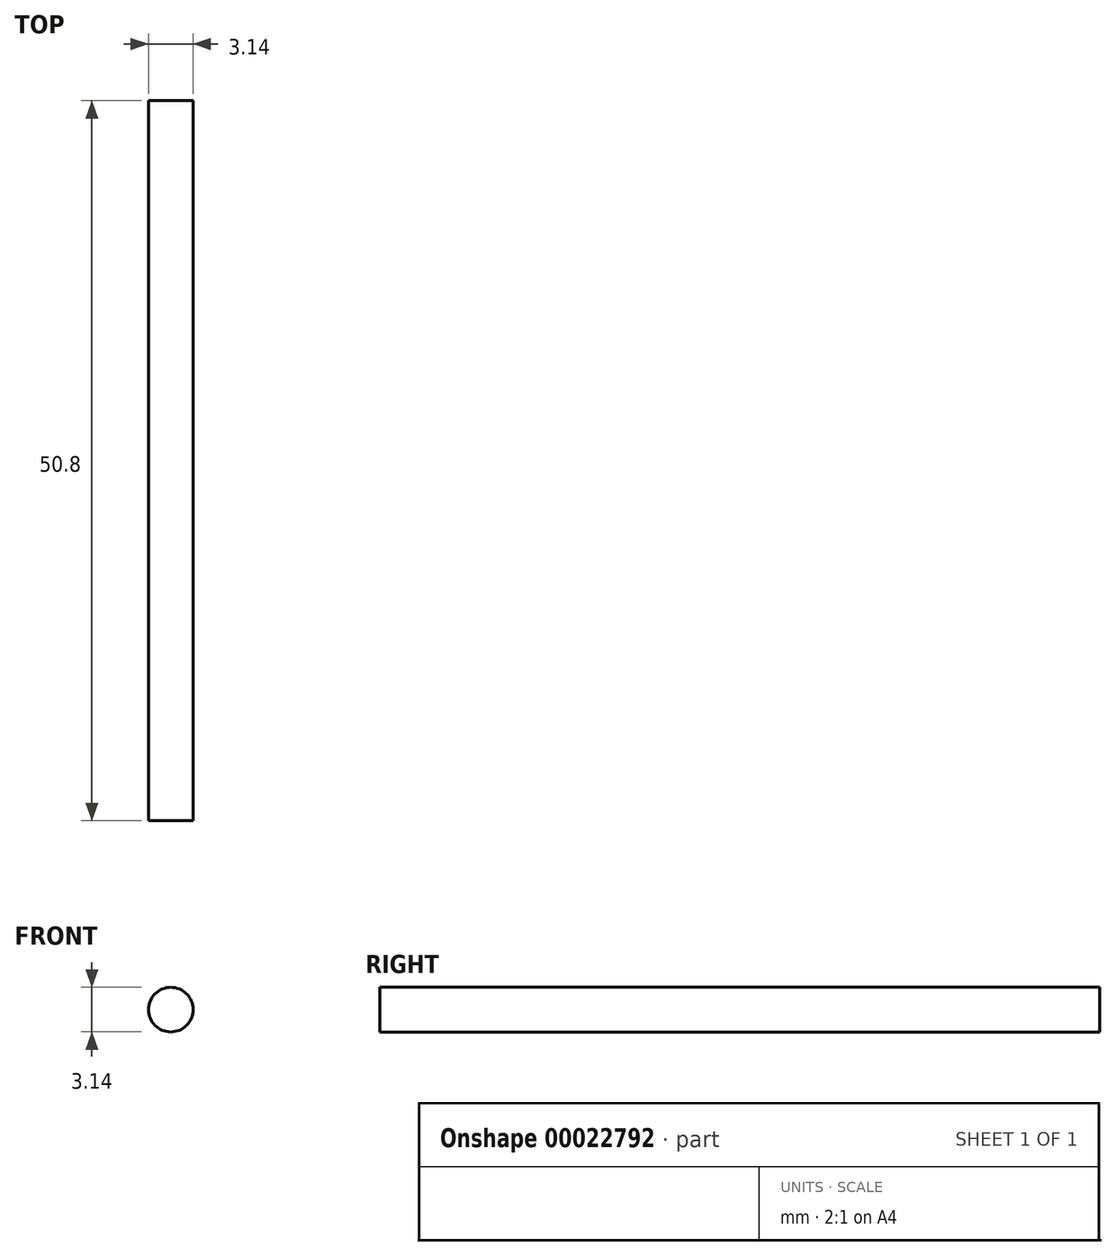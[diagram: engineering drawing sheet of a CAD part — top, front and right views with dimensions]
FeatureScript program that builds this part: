
annotation { "Feature Type Name" : "Feature", "Feature Type Description" : "" }
export const myFeature = defineFeature(function(context is Context, id is Id, definition is map)
    precondition{}
    {
        {
            var Q0;
            Q0=qCreatedBy(makeId("Front.planeOp"),FACE);
            var sketch = newSketch(context, id + "F0", { "sketchPlane" : qUnion([Q0])});
            skCircle(sketch, "E0", {"center": v(0, 0) * mm, "radius": 1.57 * mm});
            skSolve(sketch);
        }
        {
            var Q0;
            Q0=makeQuery(id+"F0.imprint","IMPRINT",FACE,{"disambiguationData":[TD([[makeQuery(id+"F0.imprint","IMPRINT",EDGE,{"derivedFrom":sQuery(id+"F0.wireOp",EDGE,"E0")}),1.0]])]});
            extrude(context, id + "F1", {"entities" : qUnion([Q0]), "depth" : 50.8 * mm});
        }
    });
